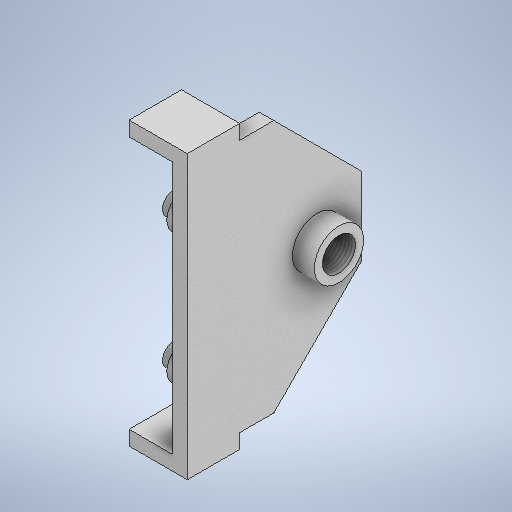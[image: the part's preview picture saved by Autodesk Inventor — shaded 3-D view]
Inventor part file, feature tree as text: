
AUTODESK INVENTOR PART (.ipt)
format: ipt  version: 2025.2 (Build 292293000, 293)  size: 384,000 bytes
history: native  units: in
note: dims shown in document units (in); Inventor stores cm internally (conversion verified against a paired STEP export)
features: extrude x7, other x4, thread x1, plane x1, hole x1, sketch x1
ambient origin geometry x8: Origin, YZ Plane, XZ Plane, XY Plane, X Axis, Y Axis, Z Axis, Center Point
bodies: Volumenkörper1 (feature_tree)
feature tree (15):
  other  "Skelett_Laufkatze.ipt"
  extrude  "Grundplatte"  Depth=0.3937in TaperAngle=0.0deg
  extrude  "Schutzwände"  Depth=0.3937in TaperAngle=0.0deg
  extrude  "Laufradaufhängung_1"  Depth=0.3937in TaperAngle=0.0deg
  extrude  "Laufradaufhängung_2"  Depth=0.3937in TaperAngle=0.0deg
  extrude  "Laufradaufhängung_3"  Depth=0.3937in TaperAngle=0.0deg
  extrude  "Laufradaufhängung_4"  Depth=0.3937in TaperAngle=0.0deg
  extrude  "Schraubbolzenöffnung"  Depth=0.3937in TaperAngle=0.0deg
  thread  "Gewinde1"  [1 undecoded]
  plane  "Arbeitsebene2"
  hole  "Bohrung1"  [1 undecoded]
  other  "Fuehrungsplatte_seite_ohne"
  other  "Fuehrungsplatte_Laufradaufhängung_ohne"
  other  "Fuehrungsplatte_Schraubbolzen_ohne"
  sketch  "Skizze5"  dims[d0=0.3937in d1=0.3937in d2=0.0in d3=0.3937in d4=0.0in d5=0.3937in d6=0.0in d7=0.3937in d8=0.0in d9=0.3937in d10=0.0in d11=0.3937in d12=0.0in d13=0.3937in d14=0.0in d15=1.9685in d16=0.0in d17=0.0in d18=0.4192in d19=0.9449in d20=0.1575in d21=0.0787in d22=90.0deg d23=1.189in d24=0.8108in]
note: 2 required parameter values undecoded (feature->parameter linkage not recoverable at this tier; creation-order binding heuristic only, values carry confidence <= 0.55)
